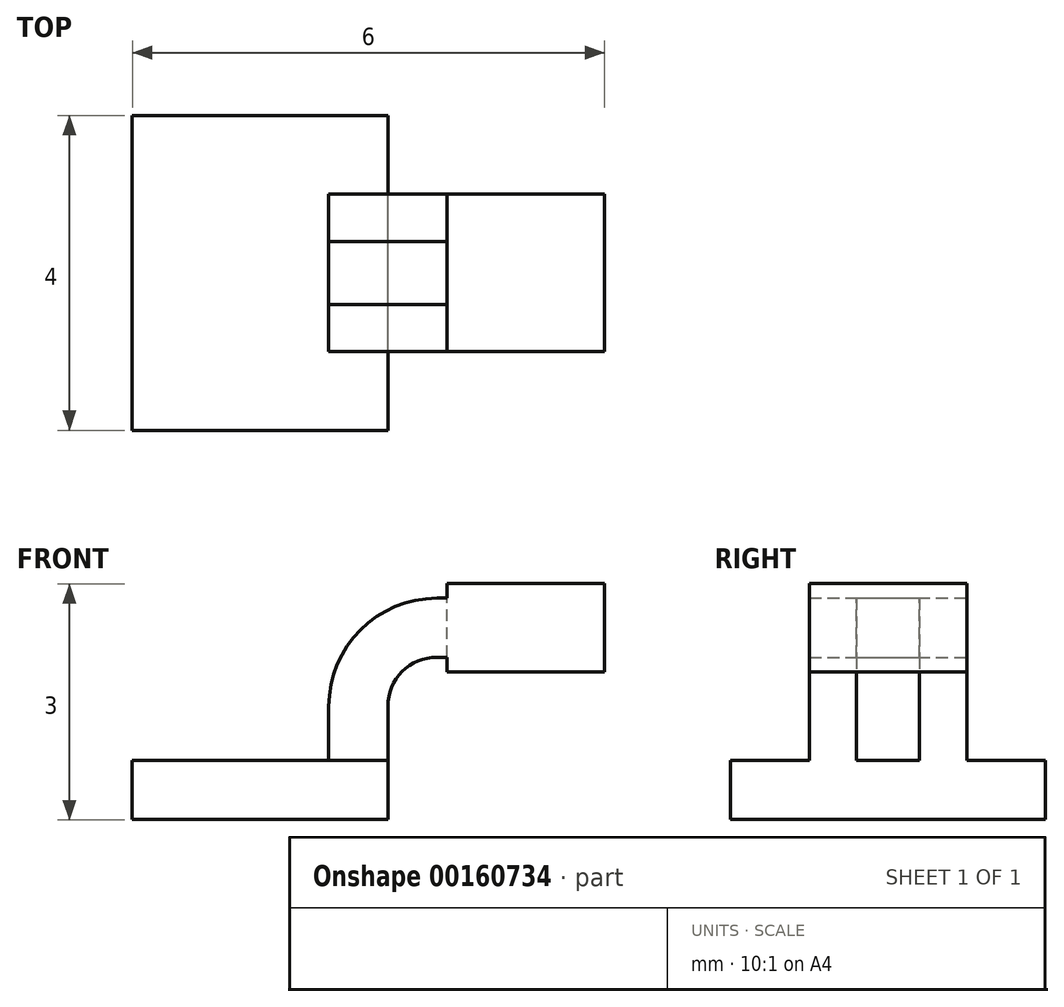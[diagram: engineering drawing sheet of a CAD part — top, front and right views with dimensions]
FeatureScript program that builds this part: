
annotation { "Feature Type Name" : "Feature", "Feature Type Description" : "" }
export const myFeature = defineFeature(function(context is Context, id is Id, definition is map)
    precondition{}
    {
        {
            var Q0;
            Q0=qCreatedBy(makeId("Front.planeOp"),FACE);
            var sketch = newSketch(context, id + "F0", { "sketchPlane" : qUnion([Q0])});
            skLineSegment(sketch, "E0.bottom", {"start": v(-1.63, 0.37) * mm, "end": v(1.63, 0.38) * mm});
            skLineSegment(sketch, "E0.top", {"start": v(-1.63, -0.38) * mm, "end": v(1.63, -0.38) * mm});
            skLineSegment(sketch, "E0.left", {"start": v(-1.63, 0.37) * mm, "end": v(-1.62, -0.38) * mm});
            skLineSegment(sketch, "E0.right", {"start": v(1.63, 0.38) * mm, "end": v(1.63, -0.37) * mm});
            skPoint(sketch, "E0.middle", {"position": v(0, 0) * mm});
            skLineSegment(sketch, "E1.bottom", {"start": v(4.38, 1.5) * mm, "end": v(2.38, 1.5) * mm});
            skLineSegment(sketch, "E1.top", {"start": v(4.38, 2.63) * mm, "end": v(2.38, 2.62) * mm});
            skLineSegment(sketch, "E1.left", {"start": v(4.38, 1.5) * mm, "end": v(4.38, 2.63) * mm});
            skLineSegment(sketch, "E1.right", {"start": v(2.38, 1.5) * mm, "end": v(2.38, 2.62) * mm});
            skPoint(sketch, "E1.middle", {"position": v(3.38, 2.06) * mm});
            skLineSegment(sketch, "E2", {"start": v(1.62, 0.38) * mm, "end": v(1.62, 1.06) * mm});
            skArc(sketch, "E3", {"start": v(1.62, 1.06) * mm, "mid": v(1.8, 1.5) * mm, "end": v(2.25, 1.69) * mm});
            skLineSegment(sketch, "E4", {"start": v(2.25, 1.69) * mm, "end": v(3.38, 1.69) * mm});
            skLineSegment(sketch, "E5.0", {"start": v(2.25, 2.44) * mm, "end": v(3.38, 2.44) * mm});
            skArc(sketch, "E5.1", {"start": v(0.87, 1.06) * mm, "mid": v(1.28, 2.04) * mm, "end": v(2.25, 2.44) * mm});
            skLineSegment(sketch, "E5.2", {"start": v(0.87, 0.38) * mm, "end": v(0.87, 1.06) * mm});
            skLineSegment(sketch, "E6", {"start": v(3.38, 1.5) * mm, "end": v(3.38, 2.63) * mm});
            skFitSpline(sketch, "E7", {"points": [v(-1.63, 0.38) * mm, v(2.25, 2.44) * mm], "startDerivative": vector(0.1, 3.6) * mm, "endDerivative": vector(5.62, 0) * mm});
            skSolve(sketch);
        }
        {
            var Q0;
            Q0=makeQuery(id+"F0.imprint","IMPRINT",FACE,{"disambiguationData":[TD([[makeQuery(id+"F0.imprint","IMPRINT",EDGE,{"derivedFrom":sQuery(id+"F0.wireOp",EDGE,"E0.top")}),1.0]])]});
            extrude(context, id + "F1", {"entities" : qUnion([Q0]), "endBound" : BoundingType.SYMMETRIC, "depth" : 4 * mm});
        }
        {
            var Q0;
            {var subQ1=sQuery(id+"F0.wireOp",EDGE,"E2");Q0=makeQuery(id+"F0.imprint","IMPRINT",FACE,{"disambiguationData":[TD([[makeQuery(id+"F0.imprint","IMPRINT",EDGE,{"derivedFrom":subQ1}),1.0]])]});}
            var Q1;
            {var subQ0=sQuery(id+"F0.wireOp",EDGE,"E1.right");var subQ1=sQuery(id+"F0.wireOp",EDGE,"E1.bottom");var subQ2=makeQuery(id+"F0.imprint","INTERSECT",VERTEX,{"derivedFrom":[subQ1,subQ0]});Q1=makeQuery(id+"F0.imprint","IMPRINT",FACE,{"disambiguationData":[TD([[makeQuery(id+"F0.imprint","IMPRINT",EDGE,{"disambiguationData":[TD([[subQ2,1.0]])],"derivedFrom":subQ1}),-1.0]])]});}
            var Q2;
            {var subQ0=sQuery(id+"F0.wireOp",EDGE,"E1.right");var subQ1=sQuery(id+"F0.wireOp",EDGE,"E1.top");var subQ2=makeQuery(id+"F0.imprint","INTERSECT",VERTEX,{"derivedFrom":[subQ1,subQ0]});Q2=makeQuery(id+"F0.imprint","IMPRINT",FACE,{"disambiguationData":[TD([[makeQuery(id+"F0.imprint","IMPRINT",EDGE,{"disambiguationData":[TD([[subQ2,1.0]])],"derivedFrom":subQ1}),1.0]])]});}
            var Q3;
            {var subQ0=sQuery(id+"F0.wireOp",EDGE,"E1.left");Q3=makeQuery(id+"F0.imprint","IMPRINT",FACE,{"disambiguationData":[TD([[makeQuery(id+"F0.imprint","IMPRINT",EDGE,{"derivedFrom":subQ0}),1.0]])]});}
            var Q4;
            {var subQ0=sQuery(id+"F0.wireOp",EDGE,"E4");var subQ1=sQuery(id+"F0.wireOp",EDGE,"E1.right");var subQ2=makeQuery(id+"F0.imprint","INTERSECT",VERTEX,{"derivedFrom":[subQ1,subQ0]});Q4=makeQuery(id+"F0.imprint","IMPRINT",FACE,{"disambiguationData":[TD([[makeQuery(id+"F0.imprint","IMPRINT",EDGE,{"disambiguationData":[TD([[subQ2,-1.0]])],"derivedFrom":subQ1}),-1.0]])]});}
            extrude(context, id + "F2", {"entities" : qUnion([Q0, Q1, Q2, Q3, Q4]), "operationType" : NewBodyOperationType.ADD, "endBound" : BoundingType.SYMMETRIC, "depth" : 2 * mm});
        }
        {
            var Q0;
            Q0=makeQuery(id+"F0.imprint","IMPRINT",FACE,{"disambiguationData":[TD([[makeQuery(id+"F0.imprint","IMPRINT",EDGE,{"derivedFrom":sQuery(id+"F0.wireOp",EDGE,"E5.1")}),1.0]])]});
            extrude(context, id + "F3", {"entities" : qUnion([Q0]), "endBound" : BoundingType.SYMMETRIC, "depth" : 0.8 * mm});
        }
    });
